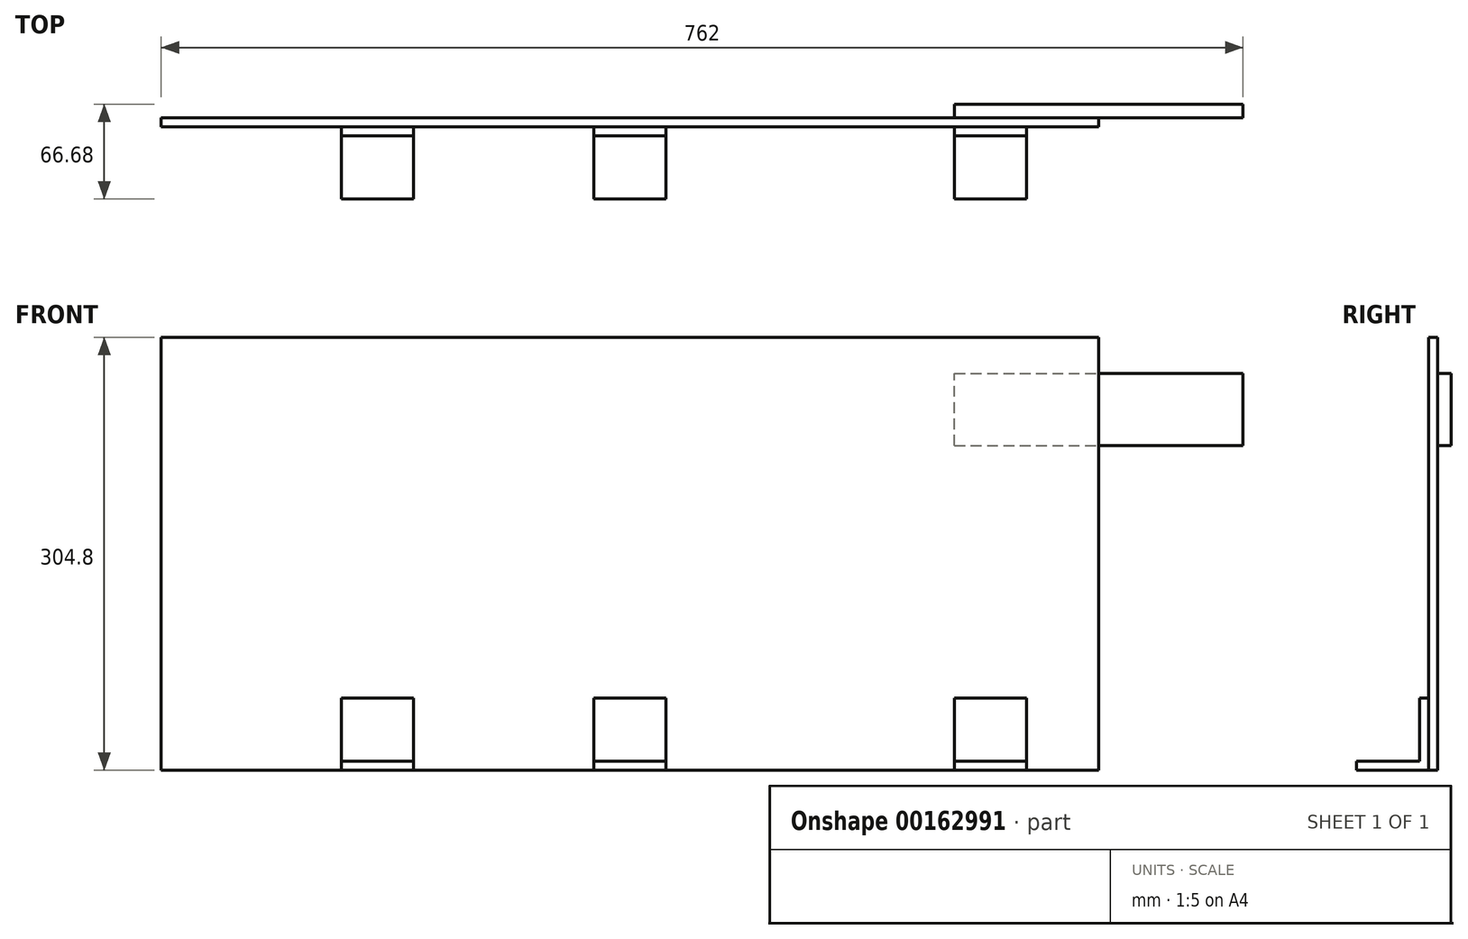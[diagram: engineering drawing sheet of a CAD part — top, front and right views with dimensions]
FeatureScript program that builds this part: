
annotation { "Feature Type Name" : "Feature", "Feature Type Description" : "" }
export const myFeature = defineFeature(function(context is Context, id is Id, definition is map)
    precondition{}
    {
        {
            var Q0;
            Q0=qCreatedBy(makeId("Front.planeOp"),FACE);
            var sketch = newSketch(context, id + "F0", { "sketchPlane" : qUnion([Q0])});
            skLineSegment(sketch, "E0.bottom", {"start": v(330.2, -152.4) * mm, "end": v(-330.2, -152.4) * mm});
            skLineSegment(sketch, "E0.top", {"start": v(330.2, 152.4) * mm, "end": v(-330.2, 152.4) * mm});
            skLineSegment(sketch, "E0.left", {"start": v(330.2, -152.4) * mm, "end": v(330.2, 152.4) * mm});
            skLineSegment(sketch, "E0.right", {"start": v(-330.2, -152.4) * mm, "end": v(-330.2, 152.4) * mm});
            skPoint(sketch, "E0.middle", {"position": v(0, 0) * mm});
            skSolve(sketch);
        }
        {
            var Q0;
            Q0=makeQuery(id+"F0.imprint","IMPRINT",FACE,{"disambiguationData":[TD([[makeQuery(id+"F0.imprint","IMPRINT",EDGE,{"derivedFrom":sQuery(id+"F0.wireOp",EDGE,"E0.bottom")}),-1.0]])]});
            extrude(context, id + "F1", {"entities" : qUnion([Q0]), "depth" : 6.35 * mm});
        }
        {
            var Q0;
            Q0=makeQuery(id+"F1.opExtrude","CAP_FACE",FACE,{"disambiguationData":[OSD([sQuery(id+"F0.wireOp",EDGE,"E0.bottom"),sQuery(id+"F0.wireOp",EDGE,"E0.top"),sQuery(id+"F0.wireOp",EDGE,"E0.left"),sQuery(id+"F0.wireOp",EDGE,"E0.right")])],"isStart":false});
            var sketch = newSketch(context, id + "F2", { "sketchPlane" : qUnion([Q0])});
            skLineSegment(sketch, "E1.bottom", {"start": v(-203.2, -152.4) * mm, "end": v(-152.4, -152.4) * mm});
            skLineSegment(sketch, "E1.top", {"start": v(-203.2, -101.6) * mm, "end": v(-152.4, -101.6) * mm});
            skLineSegment(sketch, "E1.left", {"start": v(-203.2, -152.4) * mm, "end": v(-203.2, -101.6) * mm});
            skLineSegment(sketch, "E1.right", {"start": v(-152.4, -152.4) * mm, "end": v(-152.4, -101.6) * mm});
            skLineSegment(sketch, "E2.bottom", {"start": v(228.6, -152.4) * mm, "end": v(279.4, -152.4) * mm});
            skLineSegment(sketch, "E2.top", {"start": v(228.6, -101.6) * mm, "end": v(279.4, -101.6) * mm});
            skLineSegment(sketch, "E2.left", {"start": v(228.6, -152.4) * mm, "end": v(228.6, -101.6) * mm});
            skLineSegment(sketch, "E2.right", {"start": v(279.4, -152.4) * mm, "end": v(279.4, -101.6) * mm});
            skLineSegment(sketch, "E3.bottom", {"start": v(25.4, -101.6) * mm, "end": v(-25.4, -101.6) * mm});
            skLineSegment(sketch, "E3.left", {"start": v(25.4, -101.6) * mm, "end": v(25.4, -152.4) * mm});
            skLineSegment(sketch, "E3.right", {"start": v(-25.4, -101.6) * mm, "end": v(-25.4, -152.4) * mm});
            skPoint(sketch, "E3.middle", {"position": v(0, -139.2) * mm});
            skPoint(sketch, "E3.middle.positionSnap0", {"position": v(0, -152.4) * mm});
            skPoint(sketch, "E3.centerSnap0", {"position": v(0, -152.4) * mm});
            skLineSegment(sketch, "E4", {"start": v(-25.4, -152.4) * mm, "end": v(25.4, -152.4) * mm});
            skPoint(sketch, "E3.top.end.orphan", {"position": v(-25.4, -176.82) * mm});
            skPoint(sketch, "E5.orphan", {"position": v(25.4, -176.82) * mm});
            skSolve(sketch);
        }
        {
            var Q0;
            Q0=makeQuery(id+"F2.imprint","IMPRINT",FACE,{"disambiguationData":[TD([[makeQuery(id+"F2.imprint","IMPRINT",EDGE,{"derivedFrom":sQuery(id+"F2.wireOp",EDGE,"E2.bottom")}),-1.0]])]});
            var Q1;
            Q1=makeQuery(id+"F2.imprint","IMPRINT",FACE,{"disambiguationData":[TD([[makeQuery(id+"F2.imprint","IMPRINT",EDGE,{"derivedFrom":sQuery(id+"F2.wireOp",EDGE,"E3.bottom")}),1.0]])]});
            var Q2;
            Q2=makeQuery(id+"F2.imprint","IMPRINT",FACE,{"disambiguationData":[TD([[makeQuery(id+"F2.imprint","IMPRINT",EDGE,{"derivedFrom":sQuery(id+"F2.wireOp",EDGE,"E1.bottom")}),-1.0]])]});
            extrude(context, id + "F3", {"entities" : qUnion([Q0, Q1, Q2]), "operationType" : NewBodyOperationType.ADD, "depth" : 6.35 * mm});
        }
        {
            var Q0;
            Q0=makeQuery(id+"F3.opExtrude","CAP_FACE",FACE,{"disambiguationData":[OSD([sQuery(id+"F2.wireOp",EDGE,"E1.bottom"),sQuery(id+"F2.wireOp",EDGE,"E1.top"),sQuery(id+"F2.wireOp",EDGE,"E1.left"),sQuery(id+"F2.wireOp",EDGE,"E1.right")])],"isStart":false});
            var sketch = newSketch(context, id + "F4", { "sketchPlane" : qUnion([Q0])});
            skLineSegment(sketch, "E6.bottom", {"start": v(-203.2, -146.05) * mm, "end": v(-152.4, -146.05) * mm});
            skLineSegment(sketch, "E6.top", {"start": v(-203.2, -152.4) * mm, "end": v(-152.4, -152.4) * mm});
            skLineSegment(sketch, "E6.left", {"start": v(-203.2, -146.05) * mm, "end": v(-203.2, -152.4) * mm});
            skLineSegment(sketch, "E6.right", {"start": v(-152.4, -146.05) * mm, "end": v(-152.4, -152.4) * mm});
            skSolve(sketch);
        }
        {
            var Q0;
            Q0=makeQuery(id+"F3.opExtrude","CAP_FACE",FACE,{"disambiguationData":[OSD([sQuery(id+"F2.wireOp",EDGE,"E3.bottom"),sQuery(id+"F2.wireOp",EDGE,"E3.left"),sQuery(id+"F2.wireOp",EDGE,"E3.right"),sQuery(id+"F2.wireOp",EDGE,"E4")])],"isStart":false});
            var sketch = newSketch(context, id + "F5", { "sketchPlane" : qUnion([Q0])});
            skLineSegment(sketch, "E7.bottom", {"start": v(-25.4, -146.05) * mm, "end": v(25.4, -146.05) * mm});
            skLineSegment(sketch, "E7.top", {"start": v(-25.4, -152.4) * mm, "end": v(25.4, -152.4) * mm});
            skLineSegment(sketch, "E7.left", {"start": v(-25.4, -146.05) * mm, "end": v(-25.4, -152.4) * mm});
            skLineSegment(sketch, "E7.right", {"start": v(25.4, -146.05) * mm, "end": v(25.4, -152.4) * mm});
            skSolve(sketch);
        }
        {
            var Q0;
            Q0=makeQuery(id+"F3.opExtrude","CAP_FACE",FACE,{"disambiguationData":[OSD([sQuery(id+"F2.wireOp",EDGE,"E2.bottom"),sQuery(id+"F2.wireOp",EDGE,"E2.top"),sQuery(id+"F2.wireOp",EDGE,"E2.left"),sQuery(id+"F2.wireOp",EDGE,"E2.right")])],"isStart":false});
            var sketch = newSketch(context, id + "F6", { "sketchPlane" : qUnion([Q0])});
            skLineSegment(sketch, "E8.bottom", {"start": v(228.6, -146.05) * mm, "end": v(279.4, -146.05) * mm});
            skLineSegment(sketch, "E8.top", {"start": v(228.6, -152.4) * mm, "end": v(279.4, -152.4) * mm});
            skLineSegment(sketch, "E8.left", {"start": v(228.6, -146.05) * mm, "end": v(228.6, -152.4) * mm});
            skLineSegment(sketch, "E8.right", {"start": v(279.4, -146.05) * mm, "end": v(279.4, -152.4) * mm});
            skSolve(sketch);
        }
        {
            var Q0;
            Q0=makeQuery(id+"F4.imprint","IMPRINT",FACE,{"disambiguationData":[TD([[makeQuery(id+"F4.imprint","IMPRINT",EDGE,{"derivedFrom":sQuery(id+"F4.wireOp",EDGE,"E6.bottom")}),-1.0]])]});
            var Q1;
            Q1=makeQuery(id+"F5.imprint","IMPRINT",FACE,{"disambiguationData":[TD([[makeQuery(id+"F5.imprint","IMPRINT",EDGE,{"derivedFrom":sQuery(id+"F5.wireOp",EDGE,"E7.bottom")}),-1.0]])]});
            var Q2;
            Q2=makeQuery(id+"F6.imprint","IMPRINT",FACE,{"disambiguationData":[TD([[makeQuery(id+"F6.imprint","IMPRINT",EDGE,{"derivedFrom":sQuery(id+"F6.wireOp",EDGE,"E8.bottom")}),-1.0]])]});
            extrude(context, id + "F7", {"entities" : qUnion([Q0, Q1, Q2]), "operationType" : NewBodyOperationType.ADD, "depth" : 44.45 * mm});
        }
        {
            var Q0;
            Q0=makeQuery(id+"F1.opExtrude","CAP_FACE",FACE,{"disambiguationData":[OSD([sQuery(id+"F0.wireOp",EDGE,"E0.bottom"),sQuery(id+"F0.wireOp",EDGE,"E0.top"),sQuery(id+"F0.wireOp",EDGE,"E0.left"),sQuery(id+"F0.wireOp",EDGE,"E0.right")])],"isStart":true});
            var sketch = newSketch(context, id + "F8", { "sketchPlane" : qUnion([Q0])});
            skLineSegment(sketch, "E9.bottom", {"start": v(-228.6, 76.2) * mm, "end": v(-431.8, 76.2) * mm});
            skLineSegment(sketch, "E9.top", {"start": v(-228.6, 127) * mm, "end": v(-431.8, 127) * mm});
            skLineSegment(sketch, "E9.left", {"start": v(-228.6, 76.2) * mm, "end": v(-228.6, 127) * mm});
            skLineSegment(sketch, "E9.right", {"start": v(-431.8, 76.2) * mm, "end": v(-431.8, 127) * mm});
            skPoint(sketch, "E9.middle", {"position": v(-330.2, 101.6) * mm});
            skSolve(sketch);
        }
        {
            var Q0;
            {var subQ0=sQuery(id+"F8.wireOp",EDGE,"E9.right");Q0=makeQuery(id+"F8.imprint","IMPRINT",FACE,{"disambiguationData":[TD([[makeQuery(id+"F8.imprint","IMPRINT",EDGE,{"derivedFrom":subQ0}),-1.0]])]});}
            var Q1;
            {var subQ0=sQuery(id+"F8.wireOp",EDGE,"E9.left");Q1=makeQuery(id+"F8.imprint","IMPRINT",FACE,{"disambiguationData":[TD([[makeQuery(id+"F8.imprint","IMPRINT",EDGE,{"derivedFrom":subQ0}),1.0]])]});}
            extrude(context, id + "F9", {"entities" : qUnion([Q0, Q1]), "operationType" : NewBodyOperationType.ADD, "depth" : 9.52 * mm});
        }
    });
